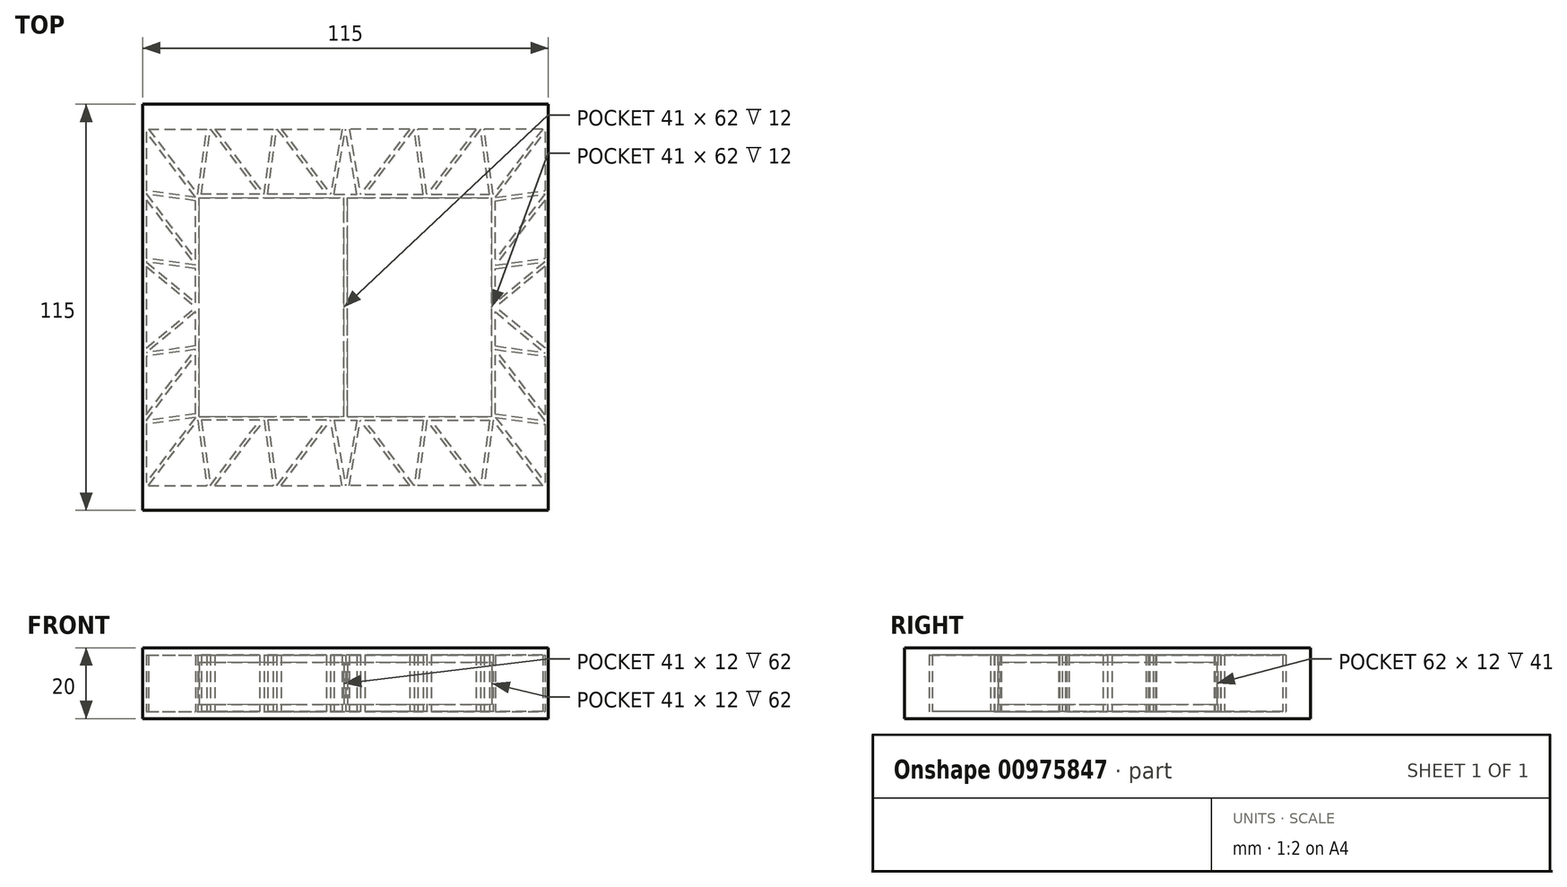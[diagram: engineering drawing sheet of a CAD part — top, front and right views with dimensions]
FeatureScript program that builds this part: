
annotation { "Feature Type Name" : "Feature", "Feature Type Description" : "" }
export const myFeature = defineFeature(function(context is Context, id is Id, definition is map)
    precondition{}
    {
        {
            var Q0;
            Q0=qCreatedBy(makeId("Top.planeOp"),FACE);
            var sketch = newSketch(context, id + "F0", { "sketchPlane" : qUnion([Q0])});
            skLineSegment(sketch, "E0.bottom", {"start": v(57.5, 57.5) * mm, "end": v(-57.5, 57.5) * mm});
            skLineSegment(sketch, "E0.top", {"start": v(57.5, -57.5) * mm, "end": v(-57.5, -57.5) * mm});
            skLineSegment(sketch, "E0.left", {"start": v(57.5, 57.5) * mm, "end": v(57.5, -57.5) * mm});
            skLineSegment(sketch, "E0.right", {"start": v(-57.5, 57.5) * mm, "end": v(-57.5, -57.5) * mm});
            skPoint(sketch, "E0.middle", {"position": v(0, 0) * mm});
            skSolve(sketch);
        }
        {
            var Q0;
            Q0 = qSketchRegion(id + "F0", true);
            extrude(context, id + "F1", {"entities" : qUnion([Q0]), "depth" : 10 * mm, "offsetDistance" : 25 * mm});
        }
        {
            var Q0;
            Q0=makeQuery(id+"F1.opExtrude","CAP_FACE",FACE,{"disambiguationData":[OSD([sQuery(id+"F0.wireOp",EDGE,"E0.bottom"),sQuery(id+"F0.wireOp",EDGE,"E0.top"),sQuery(id+"F0.wireOp",EDGE,"E0.left"),sQuery(id+"F0.wireOp",EDGE,"E0.right")])],"isStart":true});
            var sketch = newSketch(context, id + "F2", { "sketchPlane" : qUnion([Q0])});
            skLineSegment(sketch, "E1.bottom", {"start": v(-41.5, 31) * mm, "end": v(41.5, 31) * mm});
            skLineSegment(sketch, "E1.top", {"start": v(-41.5, -31) * mm, "end": v(41.5, -31) * mm});
            skLineSegment(sketch, "E1.left", {"start": v(-41.5, 31) * mm, "end": v(-41.5, -31) * mm});
            skLineSegment(sketch, "E1.right", {"start": v(41.5, 31) * mm, "end": v(41.5, -31) * mm});
            skPoint(sketch, "E1.middle", {"position": v(0, 0) * mm});
            skSolve(sketch);
        }
        {
            var Q0;
            Q0 = qSketchRegion(id + "F2", true);
            extrude(context, id + "F3", {"entities" : qUnion([Q0]), "operationType" : NewBodyOperationType.REMOVE, "oppositeDirection" : true, "depth" : 6 * mm, "offsetDistance" : 25 * mm});
        }
        {
            var Q0;
            Q0=makeQuery(id+"F1.opExtrude","CAP_FACE",FACE,{"disambiguationData":[OSD([sQuery(id+"F0.wireOp",EDGE,"E0.bottom"),sQuery(id+"F0.wireOp",EDGE,"E0.top"),sQuery(id+"F0.wireOp",EDGE,"E0.left"),sQuery(id+"F0.wireOp",EDGE,"E0.right")])],"isStart":true});
            var sketch = newSketch(context, id + "F4", { "sketchPlane" : qUnion([Q0])});
            skLineSegment(sketch, "E2.bottom", {"start": v(-0.5, 31) * mm, "end": v(0.5, 31) * mm});
            skLineSegment(sketch, "E2.top", {"start": v(-0.5, -31) * mm, "end": v(0.5, -31) * mm});
            skLineSegment(sketch, "E2.left", {"start": v(-0.5, 31) * mm, "end": v(-0.5, -31) * mm});
            skLineSegment(sketch, "E2.right", {"start": v(0.5, 31) * mm, "end": v(0.5, -31) * mm});
            skPoint(sketch, "E2.middle", {"position": v(0, 0) * mm});
            skSolve(sketch);
        }
        {
            var Q0;
            Q0 = qSketchRegion(id + "F4", true);
            extrude(context, id + "F5", {"entities" : qUnion([Q0]), "operationType" : NewBodyOperationType.ADD, "oppositeDirection" : true, "depth" : 6 * mm, "offsetDistance" : 25 * mm});
        }
        {
            var Q0;
            Q0=makeQuery(id+"F5.boolean.opBoolean","MERGE",FACE,{"derivedFrom":[makeQuery(id+"F1.opExtrude","CAP_FACE",FACE,{"disambiguationData":[OSD([sQuery(id+"F0.wireOp",EDGE,"E0.bottom"),sQuery(id+"F0.wireOp",EDGE,"E0.top"),sQuery(id+"F0.wireOp",EDGE,"E0.left"),sQuery(id+"F0.wireOp",EDGE,"E0.right")])],"isStart":true}),makeQuery(id+"F5.opExtrude","CAP_FACE",FACE,{"disambiguationData":[OSD([sQuery(id+"F4.wireOp",EDGE,"E2.bottom"),sQuery(id+"F4.wireOp",EDGE,"E2.top"),sQuery(id+"F4.wireOp",EDGE,"E2.left"),sQuery(id+"F4.wireOp",EDGE,"E2.right")])],"isStart":true})]});
            var sketch = newSketch(context, id + "F6", { "sketchPlane" : qUnion([Q0])});
            skLineSegment(sketch, "E3", {"start": v(-57.5, 56.5) * mm, "end": v(57.5, 56.5) * mm, "construction": true});
            skLineSegment(sketch, "E4", {"start": v(-57.5, 51.5) * mm, "end": v(57.5, 51.5) * mm, "construction": true});
            skLineSegment(sketch, "E5", {"start": v(-57.5, -56.5) * mm, "end": v(57.5, -56.5) * mm, "construction": true});
            skLineSegment(sketch, "E6", {"start": v(-57.5, -51.5) * mm, "end": v(57.5, -51.5) * mm, "construction": true});
            skLineSegment(sketch, "E7", {"start": v(-55.87, 50.5) * mm, "end": v(-41.87, 32) * mm});
            skLineSegment(sketch, "E8", {"start": v(-42.5, 31.17) * mm, "end": v(-56.5, 49.67) * mm});
            skLineSegment(sketch, "E9", {"start": v(-41.87, 32) * mm, "end": v(-39.31, 50.5) * mm});
            skLineSegment(sketch, "E10", {"start": v(-40.86, 32) * mm, "end": v(-38.3, 50.5) * mm});
            skLineSegment(sketch, "E11", {"start": v(-55.87, 50.5) * mm, "end": v(-39.31, 50.5) * mm});
            skLineSegment(sketch, "E12", {"start": v(-38.3, 50.5) * mm, "end": v(-24.3, 32) * mm});
            skLineSegment(sketch, "E13", {"start": v(-37.05, 50.5) * mm, "end": v(-23.05, 32) * mm});
            skLineSegment(sketch, "E14", {"start": v(-23.05, 32) * mm, "end": v(-20.49, 50.5) * mm});
            skLineSegment(sketch, "E15", {"start": v(-22.04, 32) * mm, "end": v(-19.48, 50.5) * mm});
            skLineSegment(sketch, "E16", {"start": v(-24.3, 32) * mm, "end": v(-40.86, 32) * mm});
            skLineSegment(sketch, "E17", {"start": v(-37.05, 50.5) * mm, "end": v(-20.49, 50.5) * mm});
            skLineSegment(sketch, "E18", {"start": v(-19.48, 50.5) * mm, "end": v(-5.48, 32) * mm});
            skLineSegment(sketch, "E19", {"start": v(-18.22, 50.5) * mm, "end": v(-4.22, 32) * mm});
            skLineSegment(sketch, "E20", {"start": v(-3.2, 32.02) * mm, "end": v(0, 50.5) * mm});
            skLineSegment(sketch, "E21", {"start": v(-18.22, 50.5) * mm, "end": v(-1.01, 50.5) * mm});
            skLineSegment(sketch, "E22", {"start": v(-5.48, 32) * mm, "end": v(-22.04, 32) * mm});
            skLineSegment(sketch, "E23.MirrorCS", {"start": v(3.21, 32) * mm, "end": v(0, 50.5) * mm});
            skLineSegment(sketch, "E24.MirrorCS", {"start": v(18.22, 50.5) * mm, "end": v(4.22, 32) * mm});
            skLineSegment(sketch, "E25.MirrorCS", {"start": v(19.48, 50.5) * mm, "end": v(5.48, 32) * mm});
            skLineSegment(sketch, "E26.MirrorCS", {"start": v(22.04, 32) * mm, "end": v(19.48, 50.5) * mm});
            skLineSegment(sketch, "E27.MirrorCS", {"start": v(23.05, 32) * mm, "end": v(20.49, 50.5) * mm});
            skLineSegment(sketch, "E28.MirrorCS", {"start": v(37.05, 50.5) * mm, "end": v(23.05, 32) * mm});
            skLineSegment(sketch, "E29.MirrorCS", {"start": v(38.3, 50.5) * mm, "end": v(24.3, 32) * mm});
            skLineSegment(sketch, "E30.MirrorCS", {"start": v(40.86, 32) * mm, "end": v(38.3, 50.5) * mm});
            skLineSegment(sketch, "E31.MirrorCS", {"start": v(41.87, 32) * mm, "end": v(39.31, 50.5) * mm});
            skLineSegment(sketch, "E32.MirrorCS", {"start": v(55.87, 50.5) * mm, "end": v(41.87, 32) * mm});
            skLineSegment(sketch, "E33.MirrorCS", {"start": v(42.5, 31.17) * mm, "end": v(56.5, 49.67) * mm});
            skLineSegment(sketch, "E34.MirrorCS", {"start": v(18.22, 50.5) * mm, "end": v(1.01, 50.5) * mm});
            skLineSegment(sketch, "E35.MirrorCS", {"start": v(5.48, 32) * mm, "end": v(22.04, 32) * mm});
            skLineSegment(sketch, "E36.MirrorCS", {"start": v(37.05, 50.5) * mm, "end": v(20.49, 50.5) * mm});
            skLineSegment(sketch, "E37.MirrorCS", {"start": v(24.3, 32) * mm, "end": v(40.86, 32) * mm});
            skLineSegment(sketch, "E38.MirrorCS", {"start": v(55.87, 50.5) * mm, "end": v(39.31, 50.5) * mm});
            skLineSegment(sketch, "E39", {"start": v(-42.5, 31.17) * mm, "end": v(-56.5, 33.1) * mm});
            skLineSegment(sketch, "E40", {"start": v(-42.5, 30.16) * mm, "end": v(-56.5, 32.1) * mm});
            skLineSegment(sketch, "E41", {"start": v(-56.5, 32.1) * mm, "end": v(-42.5, 13.6) * mm});
            skLineSegment(sketch, "E42", {"start": v(-56.5, 30.44) * mm, "end": v(-42.5, 11.94) * mm});
            skLineSegment(sketch, "E43", {"start": v(-42.5, 11.94) * mm, "end": v(-56.5, 13.88) * mm});
            skLineSegment(sketch, "E44", {"start": v(-42.5, 10.93) * mm, "end": v(-56.5, 12.87) * mm});
            skLineSegment(sketch, "E45", {"start": v(-56.5, 33.1) * mm, "end": v(-56.5, 49.67) * mm});
            skLineSegment(sketch, "E46", {"start": v(-42.5, 30.16) * mm, "end": v(-42.5, 13.6) * mm});
            skLineSegment(sketch, "E47", {"start": v(-56.5, 13.88) * mm, "end": v(-56.5, 30.44) * mm});
            skLineSegment(sketch, "E48.MirrorCS", {"start": v(-56.5, -30.44) * mm, "end": v(-42.5, -11.94) * mm});
            skLineSegment(sketch, "E49.MirrorCS", {"start": v(-56.5, -32.1) * mm, "end": v(-42.5, -13.6) * mm});
            skLineSegment(sketch, "E50.MirrorCS", {"start": v(-42.5, -30.16) * mm, "end": v(-56.5, -32.1) * mm});
            skLineSegment(sketch, "E51.MirrorCS", {"start": v(-42.5, -31.17) * mm, "end": v(-56.5, -33.1) * mm});
            skLineSegment(sketch, "E52.MirrorCS", {"start": v(-42.5, -31.17) * mm, "end": v(-56.5, -49.67) * mm});
            skLineSegment(sketch, "E53.MirrorCS", {"start": v(-55.87, -50.5) * mm, "end": v(-41.87, -32) * mm});
            skLineSegment(sketch, "E54", {"start": v(-42.5, -13.6) * mm, "end": v(-42.5, -30.16) * mm});
            skLineSegment(sketch, "E55.MirrorCS", {"start": v(-42.5, -11.94) * mm, "end": v(-56.5, -13.88) * mm});
            skLineSegment(sketch, "E56", {"start": v(-56.5, -30.44) * mm, "end": v(-56.5, -13.88) * mm});
            skLineSegment(sketch, "E57", {"start": v(-56.5, -49.67) * mm, "end": v(-56.5, -33.1) * mm});
            skLineSegment(sketch, "E58.MirrorCS", {"start": v(56.5, 33.1) * mm, "end": v(56.5, 49.67) * mm});
            skLineSegment(sketch, "E59.MirrorCS", {"start": v(42.5, 31.17) * mm, "end": v(56.5, 33.1) * mm});
            skLineSegment(sketch, "E60.MirrorCS", {"start": v(42.5, 30.16) * mm, "end": v(56.5, 32.1) * mm});
            skLineSegment(sketch, "E61.MirrorCS", {"start": v(42.5, 30.16) * mm, "end": v(42.5, 13.6) * mm});
            skLineSegment(sketch, "E62.MirrorCS", {"start": v(56.5, 32.1) * mm, "end": v(42.5, 13.6) * mm});
            skLineSegment(sketch, "E63.MirrorCS", {"start": v(56.5, 13.88) * mm, "end": v(56.5, 30.44) * mm});
            skLineSegment(sketch, "E64.MirrorCS", {"start": v(42.5, 11.94) * mm, "end": v(56.5, 13.88) * mm});
            skLineSegment(sketch, "E65.MirrorCS", {"start": v(42.5, -11.94) * mm, "end": v(56.5, -13.88) * mm});
            skLineSegment(sketch, "E66.MirrorCS", {"start": v(56.5, -30.44) * mm, "end": v(56.5, -13.88) * mm});
            skLineSegment(sketch, "E67.MirrorCS", {"start": v(56.5, -30.44) * mm, "end": v(42.5, -11.94) * mm});
            skLineSegment(sketch, "E68.MirrorCS", {"start": v(56.5, -32.1) * mm, "end": v(42.5, -13.6) * mm});
            skLineSegment(sketch, "E69.MirrorCS", {"start": v(42.5, -13.6) * mm, "end": v(42.5, -30.16) * mm});
            skLineSegment(sketch, "E70.MirrorCS", {"start": v(42.5, -30.16) * mm, "end": v(56.5, -32.1) * mm});
            skLineSegment(sketch, "E71.MirrorCS", {"start": v(42.5, -31.17) * mm, "end": v(56.5, -33.1) * mm});
            skLineSegment(sketch, "E72.MirrorCS", {"start": v(56.5, -49.67) * mm, "end": v(56.5, -33.1) * mm});
            skLineSegment(sketch, "E73.MirrorCS", {"start": v(42.5, -31.17) * mm, "end": v(56.5, -49.67) * mm});
            skLineSegment(sketch, "E74.MirrorCS", {"start": v(55.87, -50.5) * mm, "end": v(41.87, -32) * mm});
            skLineSegment(sketch, "E75.MirrorCS", {"start": v(-24.3, -32) * mm, "end": v(-40.86, -32) * mm});
            skLineSegment(sketch, "E76.MirrorCS", {"start": v(-38.3, -50.5) * mm, "end": v(-24.3, -32) * mm});
            skLineSegment(sketch, "E77.MirrorCS", {"start": v(-37.05, -50.5) * mm, "end": v(-23.05, -32) * mm});
            skLineSegment(sketch, "E78.MirrorCS", {"start": v(-37.05, -50.5) * mm, "end": v(-20.49, -50.5) * mm});
            skLineSegment(sketch, "E79.MirrorCS", {"start": v(-23.05, -32) * mm, "end": v(-20.49, -50.5) * mm});
            skLineSegment(sketch, "E80.MirrorCS", {"start": v(-22.04, -32) * mm, "end": v(-19.48, -50.5) * mm});
            skLineSegment(sketch, "E81.MirrorCS", {"start": v(-5.48, -32) * mm, "end": v(-22.04, -32) * mm});
            skLineSegment(sketch, "E82.MirrorCS", {"start": v(-19.48, -50.5) * mm, "end": v(-5.48, -32) * mm});
            skLineSegment(sketch, "E83.MirrorCS", {"start": v(-18.22, -50.5) * mm, "end": v(-4.22, -32) * mm});
            skLineSegment(sketch, "E84.MirrorCS", {"start": v(18.22, -50.5) * mm, "end": v(4.22, -32) * mm});
            skLineSegment(sketch, "E85.MirrorCS", {"start": v(19.48, -50.5) * mm, "end": v(5.48, -32) * mm});
            skLineSegment(sketch, "E86.MirrorCS", {"start": v(5.48, -32) * mm, "end": v(22.04, -32) * mm});
            skLineSegment(sketch, "E87.MirrorCS", {"start": v(22.04, -32) * mm, "end": v(19.48, -50.5) * mm});
            skLineSegment(sketch, "E88.MirrorCS", {"start": v(23.05, -32) * mm, "end": v(20.49, -50.5) * mm});
            skLineSegment(sketch, "E89.MirrorCS", {"start": v(37.05, -50.5) * mm, "end": v(20.49, -50.5) * mm});
            skLineSegment(sketch, "E90.MirrorCS", {"start": v(37.05, -50.5) * mm, "end": v(23.05, -32) * mm});
            skLineSegment(sketch, "E91.MirrorCS", {"start": v(38.3, -50.5) * mm, "end": v(24.3, -32) * mm});
            skLineSegment(sketch, "E92.MirrorCS", {"start": v(24.3, -32) * mm, "end": v(40.86, -32) * mm});
            skLineSegment(sketch, "E93.MirrorCS", {"start": v(40.86, -32) * mm, "end": v(38.3, -50.5) * mm});
            skLineSegment(sketch, "E94.MirrorCS", {"start": v(41.87, -32) * mm, "end": v(39.31, -50.5) * mm});
            skLineSegment(sketch, "E95.MirrorCS", {"start": v(-41.87, -32) * mm, "end": v(-39.31, -50.5) * mm});
            skLineSegment(sketch, "E96.MirrorCS", {"start": v(-40.86, -32) * mm, "end": v(-38.3, -50.5) * mm});
            skLineSegment(sketch, "E97.MirrorCS", {"start": v(-55.87, -50.5) * mm, "end": v(-39.31, -50.5) * mm});
            skLineSegment(sketch, "E98.MirrorCS", {"start": v(55.87, -50.5) * mm, "end": v(39.31, -50.5) * mm});
            skLineSegment(sketch, "E99", {"start": v(-3.2, 32.02) * mm, "end": v(3.21, 32) * mm});
            skLineSegment(sketch, "E100", {"start": v(-1.01, 50.5) * mm, "end": v(-4.22, 32) * mm});
            skLineSegment(sketch, "E101.MirrorCS", {"start": v(1.01, 50.5) * mm, "end": v(4.22, 32) * mm});
            skLineSegment(sketch, "E102.MirrorCS", {"start": v(-3.2, -32.02) * mm, "end": v(0, -50.5) * mm});
            skLineSegment(sketch, "E103.MirrorCS", {"start": v(-1.01, -50.5) * mm, "end": v(-4.22, -32) * mm});
            skLineSegment(sketch, "E104.MirrorCS", {"start": v(3.21, -32) * mm, "end": v(0, -50.5) * mm});
            skLineSegment(sketch, "E105.MirrorCS", {"start": v(1.01, -50.5) * mm, "end": v(4.22, -32) * mm});
            skLineSegment(sketch, "E106.MirrorCS", {"start": v(-3.2, -32.02) * mm, "end": v(3.21, -32) * mm});
            skLineSegment(sketch, "E107.MirrorCS", {"start": v(-18.22, -50.5) * mm, "end": v(-1.01, -50.5) * mm});
            skLineSegment(sketch, "E108.MirrorCS", {"start": v(18.22, -50.5) * mm, "end": v(1.01, -50.5) * mm});
            skLineSegment(sketch, "E109.MirrorCS", {"start": v(56.5, 30.44) * mm, "end": v(42.5, 11.94) * mm});
            skLineSegment(sketch, "E110", {"start": v(-42.5, 10.93) * mm, "end": v(-42.5, 1.3) * mm});
            skLineSegment(sketch, "E111.MirrorCS", {"start": v(42.5, 10.93) * mm, "end": v(56.5, 12.87) * mm});
            skLineSegment(sketch, "E112", {"start": v(-42.5, 1.3) * mm, "end": v(-56.5, 12.87) * mm});
            skLineSegment(sketch, "E113", {"start": v(-56.5, 11.57) * mm, "end": v(-42.5, 0) * mm});
            skLineSegment(sketch, "E114.MirrorCS", {"start": v(-56.5, -11.57) * mm, "end": v(-42.5, 0) * mm});
            skLineSegment(sketch, "E115", {"start": v(-56.5, -11.57) * mm, "end": v(-56.5, 11.57) * mm});
            skLineSegment(sketch, "E116.MirrorCS", {"start": v(42.5, 10.93) * mm, "end": v(42.5, 1.3) * mm});
            skLineSegment(sketch, "E117.MirrorCS", {"start": v(56.5, 11.57) * mm, "end": v(42.5, 0) * mm});
            skLineSegment(sketch, "E118.MirrorCS", {"start": v(56.5, -11.57) * mm, "end": v(42.5, 0) * mm});
            skLineSegment(sketch, "E119.MirrorCS", {"start": v(56.5, -11.57) * mm, "end": v(56.5, 11.57) * mm});
            skLineSegment(sketch, "E120.MirrorCS", {"start": v(42.5, 1.3) * mm, "end": v(56.5, 12.87) * mm});
            skLineSegment(sketch, "E121", {"start": v(-42.5, -1.3) * mm, "end": v(-42.5, -10.94) * mm});
            skLineSegment(sketch, "E122", {"start": v(-42.5, -10.94) * mm, "end": v(-56.5, -12.87) * mm});
            skLineSegment(sketch, "E123", {"start": v(-56.5, -12.87) * mm, "end": v(-42.5, -1.3) * mm});
            skLineSegment(sketch, "E124.MirrorCS", {"start": v(56.5, -12.87) * mm, "end": v(42.5, -1.3) * mm});
            skLineSegment(sketch, "E125.MirrorCS", {"start": v(42.5, -1.3) * mm, "end": v(42.5, -10.94) * mm});
            skLineSegment(sketch, "E126.MirrorCS", {"start": v(42.5, -10.94) * mm, "end": v(56.5, -12.87) * mm});
            skSolve(sketch);
        }
        {
            var Q0;
            Q0 = qSketchRegion(id + "F6", true);
            extrude(context, id + "F7", {"entities" : qUnion([Q0]), "operationType" : NewBodyOperationType.REMOVE, "oppositeDirection" : true, "depth" : 8 * mm, "offsetDistance" : 25 * mm});
        }
        {
            var Q0;
            Q0 = qSketchRegion(id + "F0", true);
            extrude(context, id + "F12", {"entities" : qUnion([Q0]), "oppositeDirection" : true, "depth" : 10 * mm, "offsetDistance" : 25 * mm});
        }
        {
            var Q0;
            Q0 = qSketchRegion(id + "F2", true);
            extrude(context, id + "F13", {"entities" : qUnion([Q0]), "operationType" : NewBodyOperationType.REMOVE, "depth" : 6 * mm, "offsetDistance" : 25 * mm});
        }
        {
            var Q0;
            Q0 = qSketchRegion(id + "F4", true);
            extrude(context, id + "F14", {"entities" : qUnion([Q0]), "operationType" : NewBodyOperationType.ADD, "depth" : 6 * mm, "offsetDistance" : 25 * mm});
        }
        {
            var Q0;
            Q0 = qSketchRegion(id + "F6", true);
            extrude(context, id + "F15", {"entities" : qUnion([Q0]), "operationType" : NewBodyOperationType.REMOVE, "depth" : 8 * mm, "offsetDistance" : 25 * mm});
        }
    });
